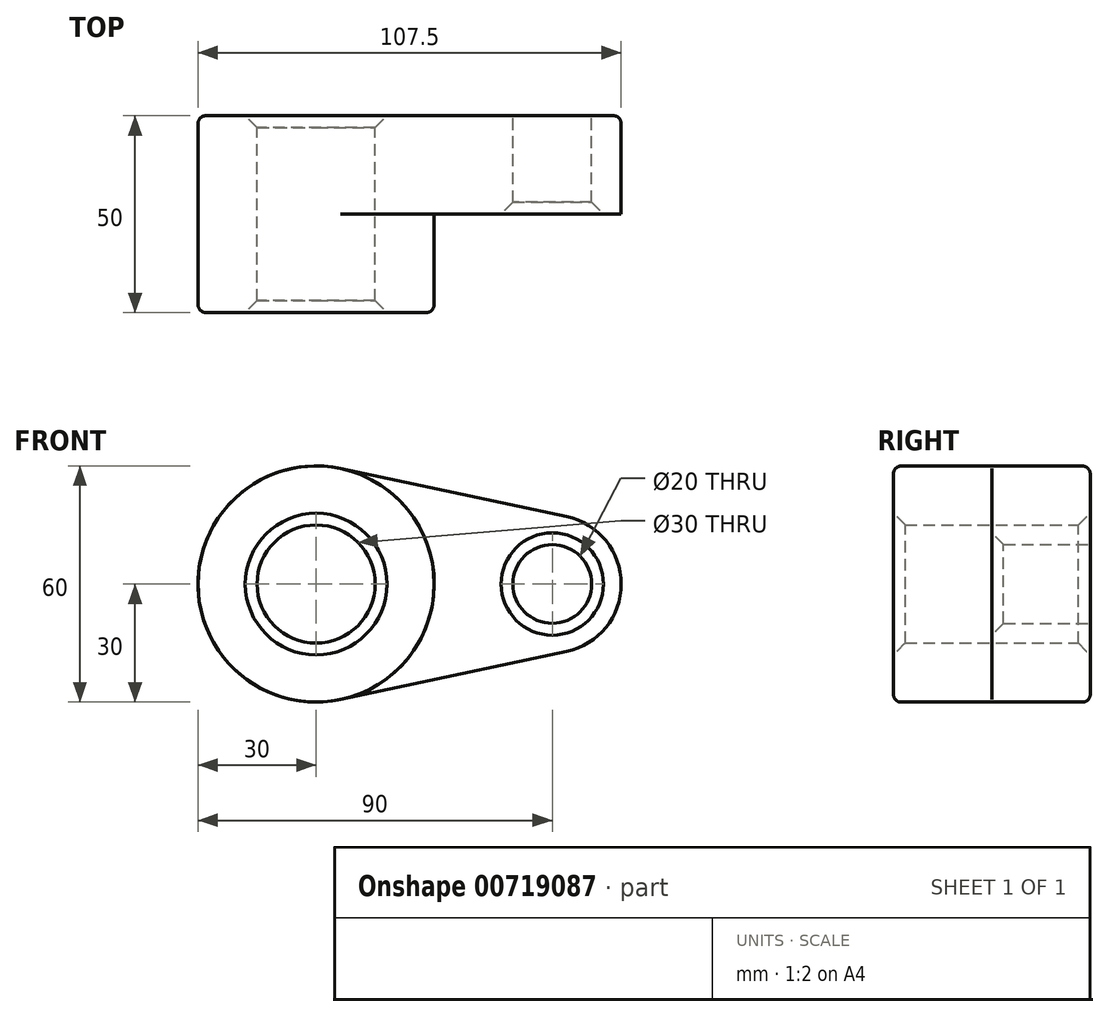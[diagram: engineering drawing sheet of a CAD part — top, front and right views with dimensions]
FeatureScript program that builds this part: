
annotation { "Feature Type Name" : "Feature", "Feature Type Description" : "" }
export const myFeature = defineFeature(function(context is Context, id is Id, definition is map)
    precondition{}
    {
        {
            var Q0;
            Q0=qCreatedBy(makeId("Front.planeOp"),FACE);
            var sketch = newSketch(context, id + "F0", { "sketchPlane" : qUnion([Q0])});
            skCircle(sketch, "E0", {"center": v(0, 0) * mm, "radius": 30 * mm});
            skCircle(sketch, "E1", {"center": v(60, 0) * mm, "radius": 17.5 * mm});
            skLineSegment(sketch, "E2", {"start": v(6.25, 29.34) * mm, "end": v(63.65, 17.12) * mm});
            skLineSegment(sketch, "E3", {"start": v(6.25, -29.34) * mm, "end": v(63.65, -17.12) * mm});
            skCircle(sketch, "E4", {"center": v(0, 0) * mm, "radius": 15 * mm});
            skCircle(sketch, "E5", {"center": v(60, 0) * mm, "radius": 10 * mm});
            skSolve(sketch);
        }
        {
            var Q0;
            {var subQ0=sQuery(id+"F0.wireOp",EDGE,"E2");Q0=makeQuery(id+"F0.imprint","IMPRINT",FACE,{"disambiguationData":[TD([[makeQuery(id+"F0.imprint","IMPRINT",EDGE,{"derivedFrom":subQ0}),-1.0]])]});}
            var Q1;
            Q1=makeQuery(id+"F0.imprint","IMPRINT",FACE,{"disambiguationData":[TD([[makeQuery(id+"F0.imprint","IMPRINT",EDGE,{"derivedFrom":sQuery(id+"F0.wireOp",EDGE,"E4")}),-1.0]])]});
            var Q2;
            Q2=makeQuery(id+"F0.imprint","IMPRINT",FACE,{"disambiguationData":[TD([[makeQuery(id+"F0.imprint","IMPRINT",EDGE,{"derivedFrom":sQuery(id+"F0.wireOp",EDGE,"E5")}),-1.0]])]});
            extrude(context, id + "F1", {"entities" : qUnion([Q0, Q1, Q2]), "depth" : 25 * mm, "offsetDistance" : 25 * mm});
        }
        {
            var Q0;
            Q0=makeQuery(id+"F0.imprint","IMPRINT",FACE,{"disambiguationData":[TD([[makeQuery(id+"F0.imprint","IMPRINT",EDGE,{"derivedFrom":sQuery(id+"F0.wireOp",EDGE,"E4")}),-1.0]])]});
            extrude(context, id + "F2", {"entities" : qUnion([Q0]), "operationType" : NewBodyOperationType.ADD, "depth" : 50 * mm, "offsetDistance" : 25 * mm});
        }
        {
            var Q0;
            Q0=makeQuery(id+"F1.opExtrude","CAP_EDGE",EDGE,{"disambiguationData":[OSD([sQuery(id+"F0.wireOp",EDGE,"E3")])],"isStart":true});
            var Q1;
            Q1=makeQuery(id+"F2.opExtrude","CAP_EDGE",EDGE,{"disambiguationData":[OSD([sQuery(id+"F0.wireOp",EDGE,"E0")])],"isStart":false});
            fillet(context, id + "F3", {"entities" : qUnion([Q0, Q1]), "radius" : 2 * mm, "tangentPropagation" : true, "allowEdgeOverflow" : false});
        }
        {
            var Q0;
            Q0=makeQuery(id+"F1.opExtrude","CAP_EDGE",EDGE,{"disambiguationData":[OSD([sQuery(id+"F0.wireOp",EDGE,"E5")])],"isStart":false});
            var Q1;
            {var subQ0=sQuery(id+"F0.wireOp",EDGE,"E4");Q1=makeQuery(id+"F2.boolean.opBoolean","MERGE",FACE,{"derivedFrom":[makeQuery(id+"F1.opExtrude","SWEPT_FACE",FACE,{"disambiguationData":[OSD([subQ0])]}),makeQuery(id+"F2.opExtrude","SWEPT_FACE",FACE,{"disambiguationData":[OSD([subQ0])]})]});}
            chamfer(context, id + "F4", {"entities" : qUnion([Q0, Q1]), "width" : 3 * mm, "tangentPropagation" : true});
        }
    });
